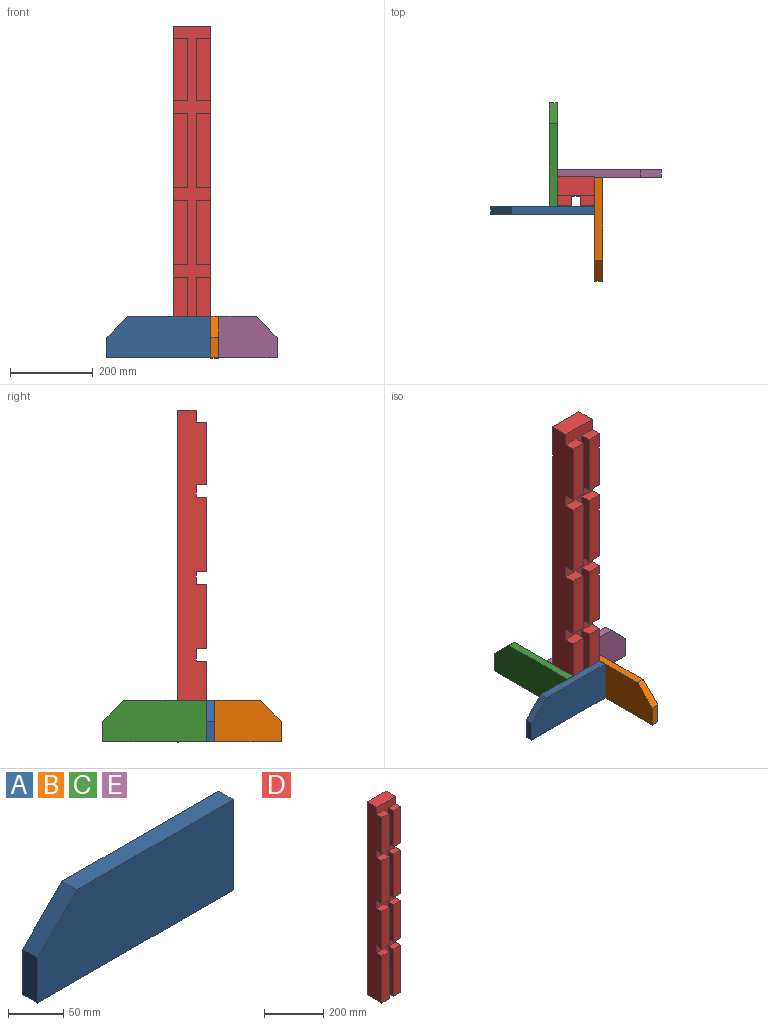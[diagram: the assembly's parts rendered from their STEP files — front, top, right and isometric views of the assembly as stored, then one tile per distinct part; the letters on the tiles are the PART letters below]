
ASSEMBLY  parts=5 mates=12
PART A: 7 faces, bbox 250x19x100 mm
  f0: plane 200x19mm, normal (0,0,1), area 3800mm2, adj f3,f4,f5,f6
  f1: plane 50x19mm, normal (-1,0,0), area 950mm2, adj f2,f4,f5,f6
  f2: plane 250x19mm, normal (0,0,-1), area 4750mm2, adj f1,f3,f4,f5
  f3: plane 100x19mm, normal (1,0,0), area 1900mm2, adj f0,f2,f4,f5
  f4: plane 250x100mm, normal (0,-1,0), area 23750mm2, adj f0,f1,f2,f3,f6
  f5: plane 250x100mm, normal (0,1,0), area 23750mm2, adj f0,f1,f2,f3,f6
  f6: plane 50x50mm, normal (-0.71,0,0.71), area 1343.5mm2, adj f0,f1,f4,f5
PART B: same geometry as A
PART C: same geometry as A
PART D: 36 faces, bbox 90x70x800 mm
  f0: plane 150x35mm, normal (0,-1,0), area 5250mm2, adj f7,f12,f27,f28
  f1: plane 180x35mm, normal (0,-1,0), area 6300mm2, adj f7,f13,f25,f26
  f2: plane 155x35mm, normal (0,-1,0), area 5425mm2, adj f7,f14,f23,f24
  f3: plane 150x35mm, normal (0,-1,0), area 5250mm2, adj f8,f9,f33,f35
  f4: plane 180x35mm, normal (0,-1,0), area 6300mm2, adj f8,f10,f31,f34
  f5: plane 155x35mm, normal (0,-1,0), area 5425mm2, adj f8,f11,f29,f32
  f6: plane 90x45mm, normal (0,0,1), area 4050mm2, adj f7,f8,f16,f21
  f7: plane 800x70mm, normal (1,0,0), area 53000mm2, adj f0,f1,f2,f6,f15,f16,f18,f21
  f8: plane 800x70mm, normal (-1,0,0), area 53000mm2, adj f3,f4,f5,f6,f16,f17,f18,f21
  f9: plane 150x25mm, normal (1,0,0), area 3750mm2, adj f3,f21,f33,f35
  f10: plane 180x25mm, normal (1,0,0), area 4500mm2, adj f4,f21,f31,f34
  f11: plane 155x25mm, normal (1,0,0), area 3875mm2, adj f5,f21,f29,f32
  f12: plane 150x25mm, normal (-1,0,0), area 3750mm2, adj f0,f21,f27,f28
  f13: plane 180x25mm, normal (-1,0,0), area 4500mm2, adj f1,f21,f25,f26
  f14: plane 155x25mm, normal (-1,0,0), area 3875mm2, adj f2,f21,f23,f24
  f15: plane 195x35mm, normal (0,-1,0), area 6825mm2, adj f7,f18,f20,f22
  f16: plane 800x90mm, normal (0,1,0), area 72000mm2, adj f6,f7,f8,f18
  f17: plane 195x35mm, normal (0,-1,0), area 6825mm2, adj f8,f18,f19,f30
  f18: plane 90x70mm, normal (0,0,-1), area 5800mm2, adj f7,f8,f15,f16,f17,f19,f20,f21
  f19: plane 195x25mm, normal (1,0,0), area 4875mm2, adj f17,f18,f21,f30
  f20: plane 195x25mm, normal (-1,0,0), area 4875mm2, adj f15,f18,f21,f22
  f21: plane 800x90mm, normal (0,-1,0), area 24400mm2, adj f6,f7,f8,f9,f10,f11,f12,f13
  f22: plane 35x25mm, normal (0,0,1), area 875mm2, adj f7,f15,f20,f21
  f23: plane 35x25mm, normal (0,0,-1), area 875mm2, adj f2,f7,f14,f21
  f24: plane 35x25mm, normal (0,0,1), area 875mm2, adj f2,f7,f14,f21
  f25: plane 35x25mm, normal (0,0,-1), area 875mm2, adj f1,f7,f13,f21
  f26: plane 35x25mm, normal (0,0,1), area 875mm2, adj f1,f7,f13,f21
  f27: plane 35x25mm, normal (0,0,-1), area 875mm2, adj f0,f7,f12,f21
  f28: plane 35x25mm, normal (0,0,1), area 875mm2, adj f0,f7,f12,f21
  f29: plane 35x25mm, normal (0,0,-1), area 875mm2, adj f5,f8,f11,f21
  f30: plane 35x25mm, normal (0,0,1), area 875mm2, adj f8,f17,f19,f21
  f31: plane 35x25mm, normal (0,0,-1), area 875mm2, adj f4,f8,f10,f21
  f32: plane 35x25mm, normal (0,0,1), area 875mm2, adj f5,f8,f11,f21
  f33: plane 35x25mm, normal (0,0,-1), area 875mm2, adj f3,f8,f9,f21
  f34: plane 35x25mm, normal (0,0,1), area 875mm2, adj f4,f8,f10,f21
  f35: plane 35x25mm, normal (0,0,1), area 875mm2, adj f3,f8,f9,f21
PART E: same geometry as A
PLACE A t=(-52.81,161.02,78.61)mm
PLACE B rot(axis=(0,0,1),90deg) t=(72.19,106.02,78.61)mm
PLACE C rot(axis=(0,0,-1),90deg) t=(-17.81,286.02,78.61)mm
PLACE D t=(27.19,196.02,28.61)mm fixed
PLACE E rot(axis=(0,0,1),180deg) t=(107.19,231.02,78.61)mm
MATE planar D.f18 <-> C.f2  axis (0,0,-1) through (27.19,197.96,28.61)mm
MATE planar E.f5 <-> D.f16  axis (0,-1,0) through (101.49,231.02,76.86)mm
MATE planar D.f18 <-> B.f2  axis (0,0,-1) through (27.19,197.96,28.61)mm
MATE planar C.f5 <-> E.f3  axis (1,0,0) through (-17.81,280.31,76.86)mm
MATE planar D.f17 <-> A.f5  axis (0,-1,0) through (-0.31,161.02,126.11)mm
MATE planar D.f7 <-> A.f3  axis (1,0,0) through (72.19,161.02,126.11)mm
MATE planar D.f7 <-> B.f5  axis (1,0,0) through (72.19,161.02,331.11)mm
MATE planar D.f8 <-> C.f5  axis (-1,0,0) through (-17.81,161.02,223.61)mm
MATE planar A.f5 <-> C.f3  axis (0,1,0) through (-127.81,161.02,128.61)mm
MATE planar D.f18 <-> A.f2  axis (0,0,-1) through (27.19,197.96,28.61)mm
MATE planar D.f16 <-> B.f3  axis (0,1,0) through (27.19,231.02,428.61)mm
MATE planar E.f2 <-> D.f18  axis (0,0,-1) through (107.19,240.52,28.61)mm
